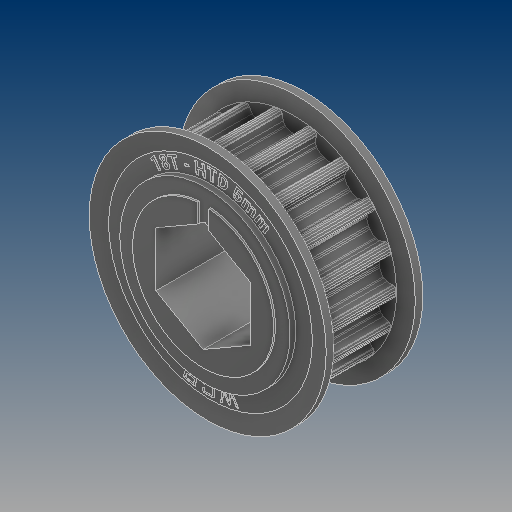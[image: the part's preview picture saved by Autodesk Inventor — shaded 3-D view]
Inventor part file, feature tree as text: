
AUTODESK INVENTOR PART (.ipt)
format: ipt  version: 2024.3 (Build 283343000, 343)  size: 819,200 bytes
history: native  units: in
note: dims shown in document units (in); Inventor stores cm internally (conversion verified against a paired STEP export)
features: mirror x2, other x1
ambient origin geometry x8: Origin, YZ Plane, XZ Plane, XY Plane, X Axis, Y Axis, Z Axis, Center Point
bodies: Solid1 (feature_tree), Solid2 (feature_tree), Solid3 (feature_tree)
feature tree (3):
  mirror  "Mirror2"
  mirror  "Mirror1"
  other  "Cut-Extrude5"
